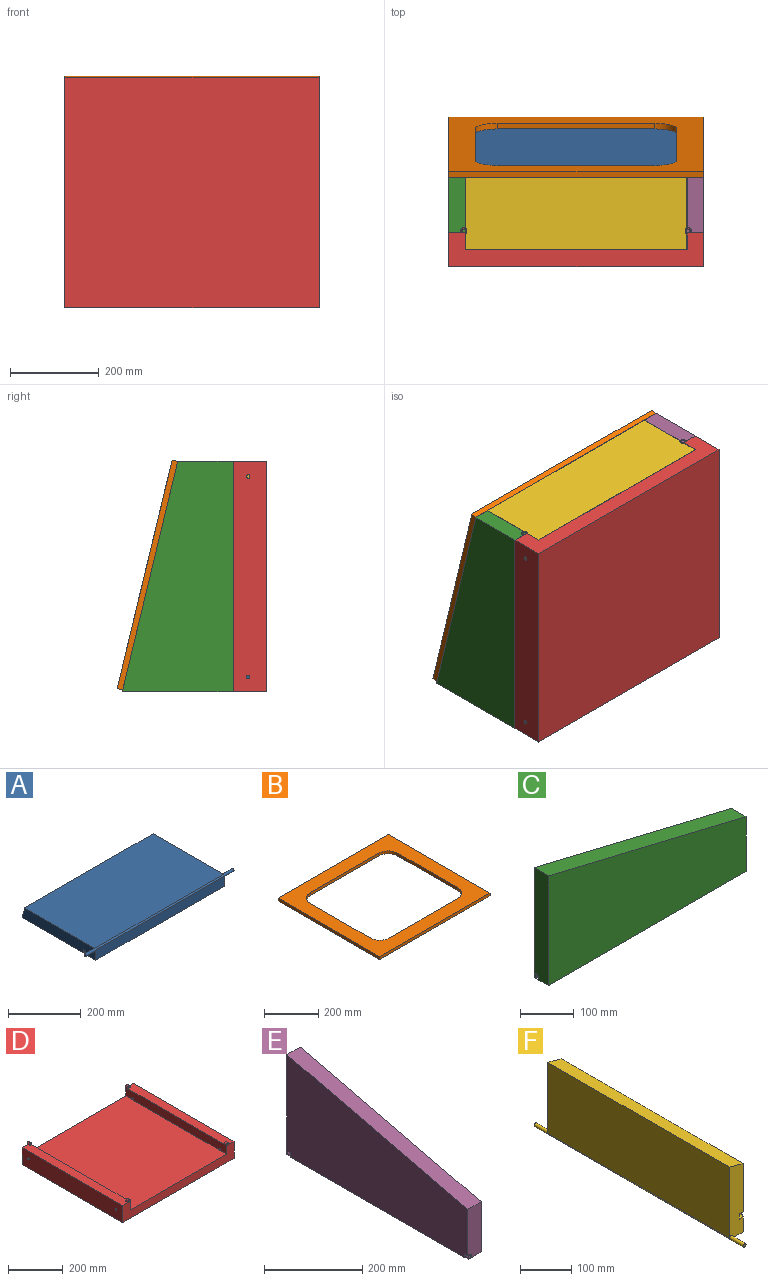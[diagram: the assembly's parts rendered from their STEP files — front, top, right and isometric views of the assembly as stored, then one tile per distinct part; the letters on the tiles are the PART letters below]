
ASSEMBLY  parts=6 mates=5
PART A: 13 faces, bbox 576x288x38 mm
  f0: plane 500x288mm, normal (0,0,-1), area 143924.1mm2, adj f1,f2,f3,f8,f10,f11
  f1: plane 288x38mm, normal (1,0,0), area 10562.9mm2, adj f0,f3,f4,f5,f8,f11,f12
  f2: plane 288x38mm, normal (-1,0,0), area 10552.3mm2, adj f0,f3,f4,f5,f8,f9,f10
  f3: plane 500x34mm, normal (0,-1,0), area 17000mm2, adj f0,f1,f2,f5
  f4: plane 500x273.45mm, normal (0,0,1), area 136723.7mm2, adj f1,f2,f5,f8
  f5: cylinder r=4mm len=576mm, axis (-1,0,0), area 5051.7mm2, adj f1,f2,f3,f4,f6,f7
  f6: plane 8x8mm, normal (1,0,0), area 50.3mm2, adj f5
  f7: plane 8x8mm, normal (-1,0,0), area 50.3mm2, adj f5
  f8: plane 500x38mm, normal (0,0.96,0.27), area 19719mm2, adj f0,f1,f2,f4
  f9: plane 13.75x4.5mm, normal (0,0,-1), area 44.6mm2, adj f2,f10
  f10: cylinder r=7.5mm len=13.75mm, axis (0,0,-1), area 173.9mm2, adj f0,f2,f9
  f11: cylinder r=7.5mm len=12.69mm, axis (0,0,-1), area 151.2mm2, adj f0,f1,f12
  f12: plane 12.69x3.5mm, normal (0,0,-1), area 31.3mm2, adj f1,f11
PART B: 14 faces, bbox 575x530x13 mm
  f0: plane 575x530mm, normal (0,0,1), area 120346mm2, adj f2,f3,f4,f5,f6,f7,f8,f9
  f1: plane 575x530mm, normal (0,0,-1), area 120346mm2, adj f2,f3,f4,f5,f6,f7,f8,f9
  f2: plane 530x13mm, normal (-1,0,0), area 6890mm2, adj f0,f1,f3,f5
  f3: plane 575x13mm, normal (0,-1,0), area 7475mm2, adj f0,f1,f2,f4
  f4: plane 530x13mm, normal (1,0,0), area 6890mm2, adj f0,f1,f3,f5
  f5: plane 575x13mm, normal (0,1,0), area 7475mm2, adj f0,f1,f2,f4
  f6: plane 310x13mm, normal (-1,0,0), area 4030mm2, adj f0,f1,f7,f13
  f7: cylinder r=50mm len=50mm, axis (0,0,1), area 1021mm2, adj f0,f1,f6,f8
  f8: plane 355x13mm, normal (0,-1,0), area 4615mm2, adj f0,f1,f7,f9
  f9: cylinder r=50mm len=50mm, axis (0,0,1), area 1021mm2, adj f0,f1,f8,f10
  f10: plane 310x13mm, normal (1,0,0), area 4030mm2, adj f0,f1,f9,f11
  f11: cylinder r=50mm len=50mm, axis (0,0,1), area 1021mm2, adj f0,f1,f10,f12
  f12: plane 355x13mm, normal (0,1,0), area 4615mm2, adj f0,f1,f11,f13
  f13: cylinder r=50mm len=50mm, axis (0,0,1), area 1021mm2, adj f0,f1,f6,f12
PART C: 16 faces, bbox 520x38x250 mm
  f0: plane 250x38mm, normal (-1,0,0), area 9392.7mm2, adj f1,f3,f4,f5,f12
  f1: plane 520x38mm, normal (0,0,-1), area 19565.1mm2, adj f0,f2,f4,f5,f7,f8,f9,f12
  f2: plane 125x38mm, normal (1,0,0), area 4642.7mm2, adj f1,f3,f4,f5,f7
  f3: plane 520x125mm, normal (0.23,0,0.97), area 20322.9mm2, adj f0,f2,f4,f5
  f4: plane 520x250mm, normal (0,-1,0), area 97500mm2, adj f0,f1,f2,f3
  f5: plane 520x250mm, normal (0,1,0), area 97305.1mm2, adj f0,f1,f2,f3,f7,f8,f9,f12
  f6: cylinder r=4mm len=10mm, axis (1,0,0), area 251.3mm2, adj f8,f9,f10
  f7: cylinder r=7mm len=11mm, axis (1,0,0), area 195.1mm2, adj f1,f2,f5,f8
  f8: plane 11x11mm, normal (1,0,0), area 53.6mm2, adj f1,f5,f6,f7
  f9: plane 4x4mm, normal (1,0,0), area 3.4mm2, adj f1,f5,f6
  f10: plane 8x8mm, normal (1,0,0), area 50.3mm2, adj f6
  f11: cylinder r=4mm len=10mm, axis (-1,0,0), area 251.3mm2, adj f13,f14,f15
  f12: cylinder r=7mm len=11mm, axis (-1,0,0), area 195.1mm2, adj f0,f1,f5,f13
  f13: plane 11x11mm, normal (-1,0,0), area 53.6mm2, adj f1,f5,f11,f12
  f14: plane 4x4mm, normal (-1,0,0), area 3.4mm2, adj f1,f5,f11
  f15: plane 8x8mm, normal (-1,0,0), area 50.3mm2, adj f11
PART D: 30 faces, bbox 575x520x87 mm
  f0: plane 520x38mm, normal (0,0,1), area 19540mm2, adj f3,f4,f5,f8,f23,f25,f27,f28
  f1: plane 520x38mm, normal (0,0,1), area 19540mm2, adj f3,f5,f6,f9,f15,f16,f19,f20
  f2: plane 520x499mm, normal (0,0,1), area 259480mm2, adj f3,f5,f8,f9
  f3: plane 575x87mm, normal (0,1,0), area 24903.6mm2, adj f0,f1,f2,f4,f6,f7,f8,f9
  f4: plane 520x76mm, normal (-1,0,0), area 39419.5mm2, adj f0,f3,f5,f7,f12,f13
  f5: plane 575x87mm, normal (0,-1,0), area 24903.6mm2, adj f0,f1,f2,f4,f6,f7,f8,f9
  f6: plane 520x76mm, normal (1,0,0), area 39419.5mm2, adj f1,f3,f5,f7,f10,f11
  f7: plane 575x520mm, normal (0,0,-1), area 299000mm2, adj f3,f4,f5,f6
  f8: plane 520x38mm, normal (1,0,0), area 19624.6mm2, adj f0,f2,f3,f5,f12,f13,f23,f24
  f9: plane 520x38mm, normal (-1,0,0), area 19624.6mm2, adj f1,f2,f3,f5,f10,f11,f14,f15
  f10: cylinder r=4mm len=38mm, axis (1,0,0), area 955mm2, adj f6,f9
  f11: cylinder r=4mm len=38mm, axis (1,0,0), area 955mm2, adj f6,f9
  f12: cylinder r=4mm len=38mm, axis (1,0,0), area 955mm2, adj f4,f8
  f13: cylinder r=4mm len=38mm, axis (1,0,0), area 955mm2, adj f4,f8
  f14: cylinder r=7mm len=14mm, axis (0,-1,0), area 287.3mm2, adj f5,f9,f15,f16
  f15: plane 14x12.74mm, normal (0,1,0), area 82.8mm2, adj f1,f9,f14,f16,f17
  f16: plane 10x4mm, normal (1,0,0), area 40mm2, adj f1,f5,f14,f15
  f17: cylinder r=4mm len=10mm, axis (0,-1,0), area 251.3mm2, adj f5,f15
  f18: cylinder r=7mm len=14mm, axis (0,1,0), area 287.3mm2, adj f3,f9,f19,f20
  f19: plane 14x12.74mm, normal (0,-1,0), area 82.8mm2, adj f1,f9,f18,f20,f21
  f20: plane 10x4mm, normal (1,0,0), area 40mm2, adj f1,f3,f18,f19
  f21: cylinder r=4mm len=10mm, axis (0,1,0), area 251.3mm2, adj f3,f19
  f22: cylinder r=4mm len=10mm, axis (0,1,0), area 251.3mm2, adj f3,f23
  f23: plane 14x12.74mm, normal (0,-1,0), area 82.8mm2, adj f0,f8,f22,f24,f25
  f24: cylinder r=7mm len=14mm, axis (0,1,0), area 287.3mm2, adj f3,f8,f23,f25
  f25: plane 10x4mm, normal (-1,0,0), area 40mm2, adj f0,f3,f23,f24
  f26: cylinder r=7mm len=14mm, axis (0,-1,0), area 287.3mm2, adj f5,f8,f27,f28
  f27: plane 14x12.74mm, normal (0,1,0), area 82.8mm2, adj f0,f8,f26,f28,f29
  f28: plane 10x4mm, normal (-1,0,0), area 40mm2, adj f0,f5,f26,f27
  f29: cylinder r=4mm len=10mm, axis (0,-1,0), area 251.3mm2, adj f5,f27
PART E: 16 faces, bbox 38x520x250 mm
  f0: plane 250x38mm, normal (0,1,0), area 9392.7mm2, adj f2,f3,f4,f5,f12
  f1: plane 125x38mm, normal (0,-1,0), area 4642.7mm2, adj f2,f3,f4,f5,f7
  f2: plane 520x38mm, normal (0,0,-1), area 19565.1mm2, adj f0,f1,f4,f5,f7,f8,f9,f12
  f3: plane 520x125mm, normal (0,-0.23,0.97), area 20322.9mm2, adj f0,f1,f4,f5
  f4: plane 520x250mm, normal (1,0,0), area 97500mm2, adj f0,f1,f2,f3
  f5: plane 520x250mm, normal (-1,0,0), area 97305.1mm2, adj f0,f1,f2,f3,f7,f8,f9,f12
  f6: cylinder r=4mm len=10mm, axis (0,-1,0), area 251.3mm2, adj f8,f9,f10
  f7: cylinder r=7mm len=11mm, axis (0,-1,0), area 195.1mm2, adj f1,f2,f5,f8
  f8: plane 11x11mm, normal (0,-1,0), area 53.6mm2, adj f2,f5,f6,f7
  f9: plane 4x4mm, normal (0,-1,0), area 3.4mm2, adj f2,f5,f6
  f10: plane 8x8mm, normal (0,-1,0), area 50.3mm2, adj f6
  f11: cylinder r=4mm len=10mm, axis (0,1,0), area 251.3mm2, adj f13,f14,f15
  f12: cylinder r=7mm len=11mm, axis (0,1,0), area 195.1mm2, adj f0,f2,f5,f13
  f13: plane 11x11mm, normal (0,1,0), area 53.6mm2, adj f2,f5,f11,f12
  f14: plane 4x4mm, normal (0,1,0), area 3.4mm2, adj f2,f5,f11
  f15: plane 8x8mm, normal (0,1,0), area 50.3mm2, adj f11
PART F: 13 faces, bbox 38x576x173.6 mm
  f0: plane 173.55x38mm, normal (0,-1,0), area 6213.9mm2, adj f1,f3,f4,f5,f6,f11,f12
  f1: plane 500x34mm, normal (0,0,-1), area 17000mm2, adj f0,f2,f3,f6
  f2: plane 173.55x38mm, normal (0,1,0), area 6203.3mm2, adj f1,f3,f4,f5,f6,f9,f10
  f3: plane 500x163mm, normal (1,0,0), area 81424.1mm2, adj f0,f1,f2,f5,f10,f11
  f4: plane 500x169.55mm, normal (-1,0,0), area 84776.3mm2, adj f0,f2,f5,f6
  f5: plane 500x38mm, normal (0.27,0,0.96), area 19719mm2, adj f0,f2,f3,f4
  f6: cylinder r=4mm len=576mm, axis (0,-1,0), area 5051.7mm2, adj f0,f1,f2,f4,f7,f8
  f7: plane 8x8mm, normal (0,1,0), area 50.3mm2, adj f6
  f8: plane 8x8mm, normal (0,-1,0), area 50.3mm2, adj f6
  f9: plane 13.75x4.5mm, normal (1,0,0), area 44.6mm2, adj f2,f10
  f10: cylinder r=7.5mm len=13.75mm, axis (1,0,0), area 173.9mm2, adj f2,f3,f9
  f11: cylinder r=7.5mm len=12.69mm, axis (1,0,0), area 151.2mm2, adj f0,f3,f12
  f12: plane 12.69x3.5mm, normal (1,0,0), area 31.3mm2, adj f0,f11
PLACE A rot(axis=(1,0,0),0deg) t=(-256.16,484.99,-54.4)mm
PLACE B rot(axis=(-1,0,0),76.5deg) t=(-255.66,559.93,207.94)mm
PLACE C rot(axis=(-0.58,-0.58,-0.58),120deg) t=(-505.16,372.99,240.6)mm
PLACE D rot(axis=(-1,0,0),90deg) t=(-255.66,296.99,205.6)mm
PLACE E rot(axis=(-1,0,0),90deg) t=(-6.16,372.99,170.6)mm
PLACE F rot(axis=(-0.58,-0.58,-0.58),120deg) t=(-255.16,424.99,427.6)mm
MATE revolute E.f6 <-> D.f14  axis (0,0,1) through (-2.16,376.99,465.6)mm
MATE fastened B.f1 <-> E.f3  axis (0,-0.97,-0.23) through (31.84,497.99,465.6)mm
MATE revolute F.f6 <-> D.f10  axis (-1,0,0) through (-543.16,338.99,431.6)mm
MATE revolute C.f6 <-> D.f22  axis (0,0,1) through (-509.16,376.99,465.6)mm
MATE revolute A.f5 <-> D.f11  axis (1,0,0) through (31.84,338.99,-20.4)mm
